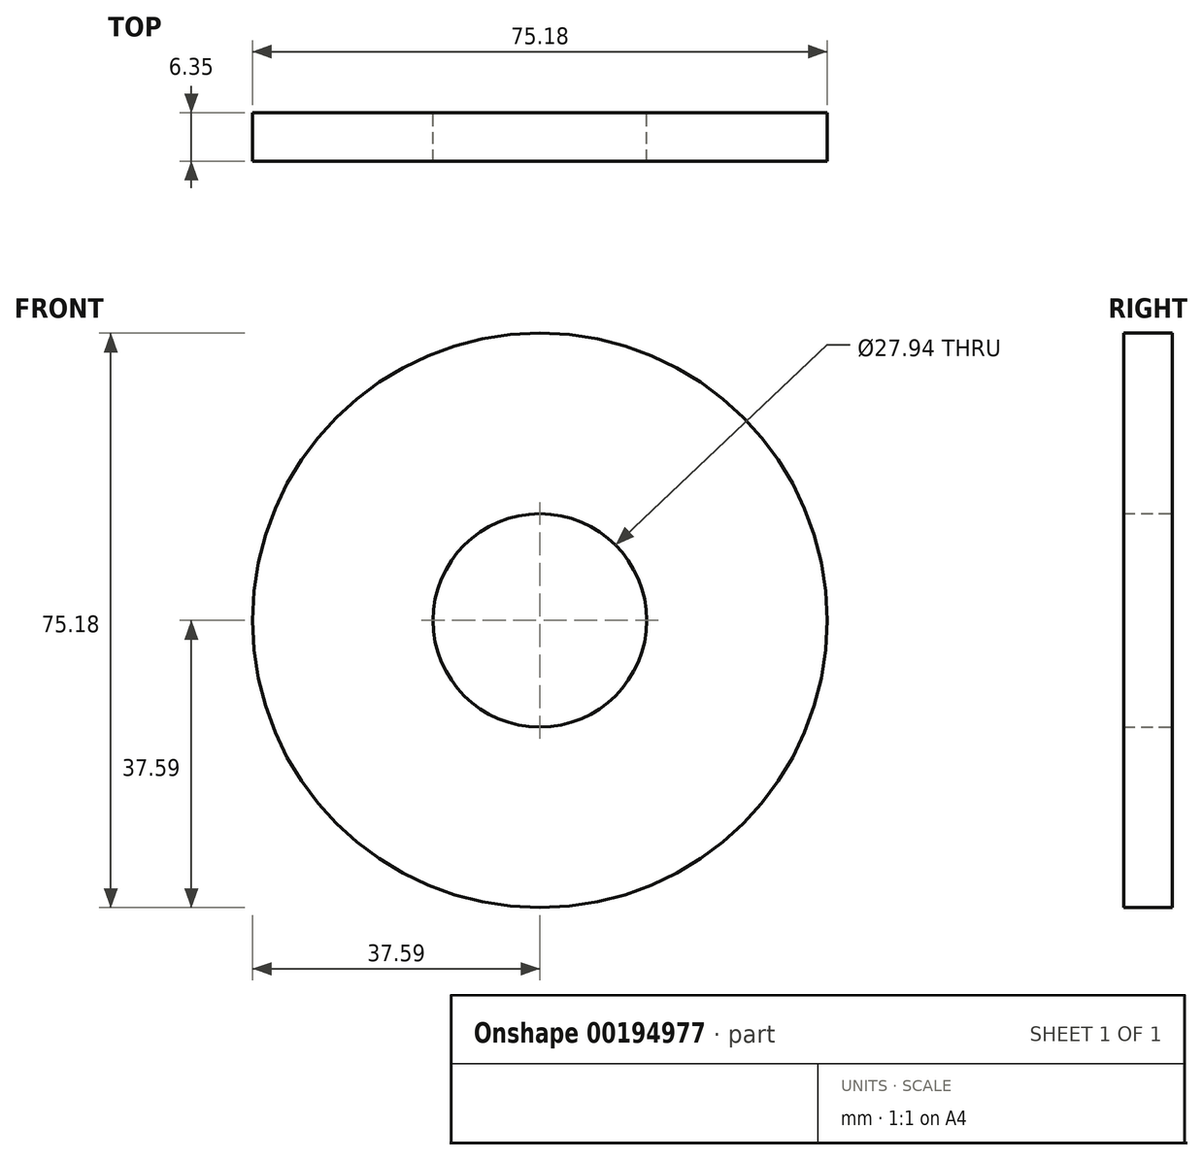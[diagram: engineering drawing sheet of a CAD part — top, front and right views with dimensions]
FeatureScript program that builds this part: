
annotation { "Feature Type Name" : "Feature", "Feature Type Description" : "" }
export const myFeature = defineFeature(function(context is Context, id is Id, definition is map)
    precondition{}
    {
        {
            var Q0;
            Q0=qCreatedBy(makeId("Front.planeOp"),FACE);
            var sketch = newSketch(context, id + "F0", { "sketchPlane" : qUnion([Q0])});
            skCircle(sketch, "E0", {"center": v(0, 0) * mm, "radius": 37.6 * mm});
            skCircle(sketch, "E1", {"center": v(0, 0) * mm, "radius": 13.97 * mm});
            skSolve(sketch);
        }
        {
            var Q0;
            Q0 = qSketchRegion(id + "F0", true);
            extrude(context, id + "F1", {"entities" : qUnion([Q0]), "depth" : 6.35 * mm});
        }
    });
